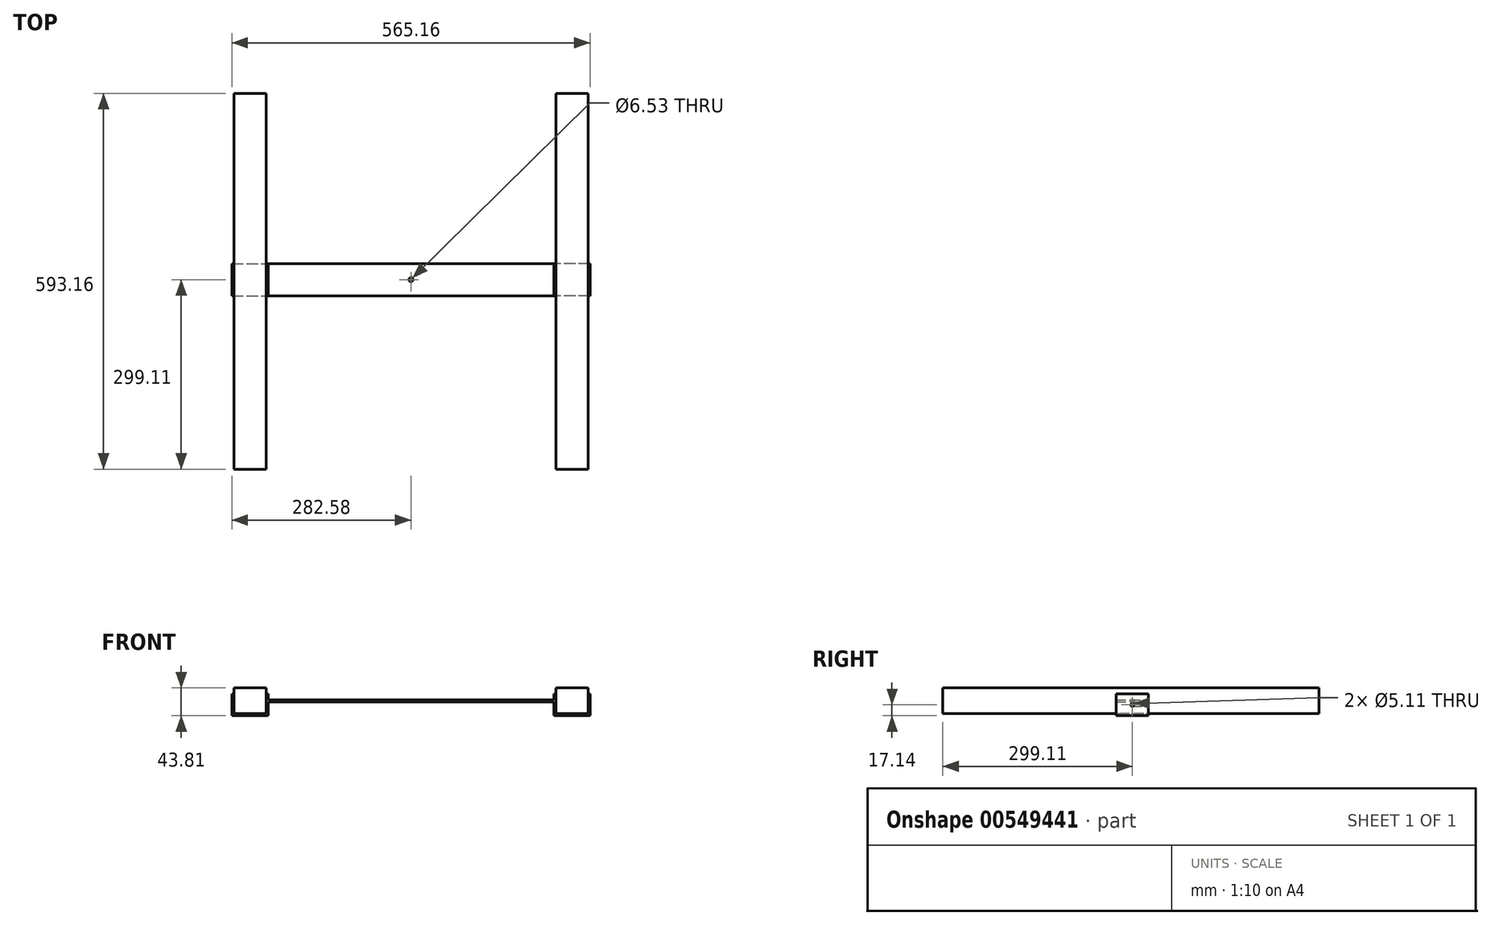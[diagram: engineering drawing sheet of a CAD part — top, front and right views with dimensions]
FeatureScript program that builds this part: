
annotation { "Feature Type Name" : "Feature", "Feature Type Description" : "" }
export const myFeature = defineFeature(function(context is Context, id is Id, definition is map)
    precondition{}
    {
        {
            var Q0;
            Q0=qCreatedBy(makeId("Top.planeOp"),FACE);
            var sketch = newSketch(context, id + "F0", { "sketchPlane" : qUnion([Q0])});
            skLineSegment(sketch, "E0.bottom", {"start": v(-279.4, 294.05) * mm, "end": v(-228.6, 294.05) * mm});
            skLineSegment(sketch, "E0.top", {"start": v(-279.4, -299.1) * mm, "end": v(-228.6, -299.1) * mm});
            skLineSegment(sketch, "E0.left", {"start": v(-279.4, 294.05) * mm, "end": v(-279.4, -299.1) * mm});
            skLineSegment(sketch, "E0.right", {"start": v(-228.6, 294.05) * mm, "end": v(-228.6, -299.1) * mm});
            skLineSegment(sketch, "E1.MirrorCS", {"start": v(279.4, 294.05) * mm, "end": v(228.6, 294.05) * mm});
            skLineSegment(sketch, "E2.MirrorCS", {"start": v(228.6, 294.05) * mm, "end": v(228.6, -299.1) * mm});
            skLineSegment(sketch, "E3.MirrorCS", {"start": v(279.4, 294.05) * mm, "end": v(279.4, -299.1) * mm});
            skLineSegment(sketch, "E4.MirrorCS", {"start": v(279.4, -299.1) * mm, "end": v(228.6, -299.1) * mm});
            skSolve(sketch);
        }
        {
            var Q0;
            Q0 = qSketchRegion(id + "F0", true);
            extrude(context, id + "F1", {"entities" : qUnion([Q0]), "depth" : 40.64 * mm, "offsetDistance" : 25.4 * mm});
        }
        {
            var Q0;
            Q0=qCreatedBy(makeId("Front.planeOp"),FACE);
            var sketch = newSketch(context, id + "F2", { "sketchPlane" : qUnion([Q0])});
            skLineSegment(sketch, "E5.0.0", {"start": v(-279.4, 0) * mm, "end": v(-228.6, 0) * mm});
            skLineSegment(sketch, "E5.0.1", {"start": v(-228.6, 0) * mm, "end": v(-228.6, 40.64) * mm});
            skLineSegment(sketch, "E5.0.2", {"start": v(-228.6, 40.64) * mm, "end": v(-279.4, 40.64) * mm});
            skLineSegment(sketch, "E5.0.3", {"start": v(-279.4, 40.64) * mm, "end": v(-279.4, 0) * mm});
            skLineSegment(sketch, "E6.0", {"start": v(-225.43, -3.17) * mm, "end": v(-225.43, 31.12) * mm});
            skLineSegment(sketch, "E6.1", {"start": v(-282.57, -3.17) * mm, "end": v(-225.43, -3.17) * mm});
            skLineSegment(sketch, "E6.2", {"start": v(-282.57, 31.12) * mm, "end": v(-282.57, -3.17) * mm});
            skLineSegment(sketch, "E7", {"start": v(-282.57, 31.12) * mm, "end": v(-279.4, 31.12) * mm});
            skLineSegment(sketch, "E8", {"start": v(-228.6, 31.12) * mm, "end": v(-225.43, 31.12) * mm});
            skLineSegment(sketch, "E9.MirrorCS", {"start": v(282.57, 31.12) * mm, "end": v(279.4, 31.12) * mm});
            skLineSegment(sketch, "E10.MirrorCS", {"start": v(282.57, 31.12) * mm, "end": v(282.57, -3.17) * mm});
            skLineSegment(sketch, "E11.MirrorCS", {"start": v(228.6, 31.12) * mm, "end": v(225.43, 31.12) * mm});
            skLineSegment(sketch, "E12.MirrorCS", {"start": v(225.43, -3.17) * mm, "end": v(225.43, 31.12) * mm});
            skLineSegment(sketch, "E13.MirrorCS", {"start": v(282.57, -3.17) * mm, "end": v(225.43, -3.17) * mm});
            skLineSegment(sketch, "E14", {"start": v(-225.43, 21.6) * mm, "end": v(225.43, 21.6) * mm});
            skPoint(sketch, "E14.endSnap0", {"position": v(225.43, 13.97) * mm});
            skLineSegment(sketch, "E15.0", {"start": v(-225.43, 18.42) * mm, "end": v(225.43, 18.42) * mm});
            skLineSegment(sketch, "E16.MirrorCS", {"start": v(228.6, 0) * mm, "end": v(228.6, 40.64) * mm});
            skLineSegment(sketch, "E17.MirrorCS", {"start": v(279.4, 0) * mm, "end": v(228.6, 0) * mm});
            skLineSegment(sketch, "E18.MirrorCS", {"start": v(279.4, 40.64) * mm, "end": v(279.4, 0) * mm});
            skSolve(sketch);
        }
        {
            var Q0;
            {var subQ0=sQuery(id+"F2.wireOp",EDGE,"E14");Q0=makeQuery(id+"F2.imprint","IMPRINT",FACE,{"disambiguationData":[TD([[makeQuery(id+"F2.imprint","IMPRINT",EDGE,{"derivedFrom":subQ0}),-1.0]])]});}
            var Q1;
            {var subQ4=sQuery(id+"F2.wireOp",EDGE,"E5.0.0");Q1=makeQuery(id+"F2.imprint","IMPRINT",FACE,{"disambiguationData":[TD([[makeQuery(id+"F2.imprint","IMPRINT",EDGE,{"derivedFrom":subQ4}),-1.0]])]});}
            var Q2;
            {var subQ4=sQuery(id+"F2.wireOp",EDGE,"E9.MirrorCS");Q2=makeQuery(id+"F2.imprint","IMPRINT",FACE,{"disambiguationData":[TD([[makeQuery(id+"F2.imprint","IMPRINT",EDGE,{"derivedFrom":subQ4}),1.0]])]});}
            extrude(context, id + "F3", {"entities" : qUnion([Q0, Q1, Q2]), "depth" : 50.8 * mm, "offsetDistance" : 25.4 * mm, "symmetric" : true});
        }
        {
            var Q0;
            Q0=makeQuery(id+"F3.opExtrude","SWEPT_FACE",FACE,{"disambiguationData":[OSD([sQuery(id+"F2.wireOp",EDGE,"E15.0")])]});
            var sketch = newSketch(context, id + "F4", { "sketchPlane" : qUnion([Q0])});
            skPoint(sketch, "E19", {"position": v(0, 0) * mm});
            skSolve(sketch);
        }
        {
            var Q0;
            Q0=sQuery(id+"F4.wireOp",VERTEX,"E19");
            var Q1;
            Q1=makeQuery(id+"F3.opExtrude","SWEPT_BODY",BODY,{"disambiguationData":[OSD([sQuery(id+"F2.wireOp",EDGE,"E5.0.0"),sQuery(id+"F2.wireOp",EDGE,"E5.0.1"),sQuery(id+"F2.wireOp",EDGE,"E5.0.3"),sQuery(id+"F2.wireOp",EDGE,"E6.0"),sQuery(id+"F2.wireOp",EDGE,"E6.1"),sQuery(id+"F2.wireOp",EDGE,"E6.2"),sQuery(id+"F2.wireOp",EDGE,"E7"),sQuery(id+"F2.wireOp",EDGE,"E8"),sQuery(id+"F2.wireOp",EDGE,"E9.MirrorCS"),sQuery(id+"F2.wireOp",EDGE,"E10.MirrorCS"),sQuery(id+"F2.wireOp",EDGE,"E11.MirrorCS"),sQuery(id+"F2.wireOp",EDGE,"E12.MirrorCS"),sQuery(id+"F2.wireOp",EDGE,"E13.MirrorCS"),sQuery(id+"F2.wireOp",EDGE,"E14"),sQuery(id+"F2.wireOp",EDGE,"E15.0"),sQuery(id+"F2.wireOp",EDGE,"E16.MirrorCS"),sQuery(id+"F2.wireOp",EDGE,"E17.MirrorCS"),sQuery(id+"F2.wireOp",EDGE,"E18.MirrorCS")])]});
            hole(context, id + "F5", {"style" : HoleStyle.SIMPLE, "endStyle" : HoleEndStyle.BLIND, "standardTappedOrClearance" : lookupTablePath({ "standard" : "ANSI", "engagement" : "75%", "pitch" : "18 tpi", "size" : "5/16", "type" : "Tapped" }), "standardBlindInLast" : lookupTablePath({ "standard" : "ANSI", "engagement" : "75%", "pitch" : "18 tpi", "size" : "5/16", "type" : "Tapped" }), "holeDiameter" : 6.53 * mm, "majorDiameter" : 7.94 * mm, "showTappedDepth" : true, "holeDepth" : 48.69 * mm, "isTappedThrough" : true, "tappedDepth" : 44.46 * mm, "tapClearance" : 3, "startFromSketch" : true, "locations" : qUnion([Q0]), "scope" : qUnion([Q1])});
        }
        {
            var Q0;
            Q0=makeQuery(id+"F3.opExtrude","SWEPT_FACE",FACE,{"disambiguationData":[OSD([sQuery(id+"F2.wireOp",EDGE,"E6.2")])]});
            var sketch = newSketch(context, id + "F6", { "sketchPlane" : qUnion([Q0])});
            skLineSegment(sketch, "E20.0.0", {"start": v(-25.4, 31.12) * mm, "end": v(-25.4, -3.17) * mm});
            skLineSegment(sketch, "E20.0.1", {"start": v(-25.4, -3.17) * mm, "end": v(25.4, -3.17) * mm});
            skLineSegment(sketch, "E20.0.2", {"start": v(25.4, -3.17) * mm, "end": v(25.4, 31.12) * mm});
            skLineSegment(sketch, "E20.0.3", {"start": v(25.4, 31.12) * mm, "end": v(-25.4, 31.12) * mm});
            skPoint(sketch, "E21", {"position": v(0, 13.97) * mm});
            skPoint(sketch, "E21.positionSnap0", {"position": v(-25.4, 13.97) * mm});
            skSolve(sketch);
        }
        {
            var Q0;
            Q0=sQuery(id+"F6.wireOp",VERTEX,"E21");
            var Q1;
            Q1=makeQuery(id+"F3.opExtrude","SWEPT_BODY",BODY,{"disambiguationData":[OSD([sQuery(id+"F2.wireOp",EDGE,"E5.0.0"),sQuery(id+"F2.wireOp",EDGE,"E5.0.1"),sQuery(id+"F2.wireOp",EDGE,"E5.0.3"),sQuery(id+"F2.wireOp",EDGE,"E6.0"),sQuery(id+"F2.wireOp",EDGE,"E6.1"),sQuery(id+"F2.wireOp",EDGE,"E6.2"),sQuery(id+"F2.wireOp",EDGE,"E7"),sQuery(id+"F2.wireOp",EDGE,"E8"),sQuery(id+"F2.wireOp",EDGE,"E9.MirrorCS"),sQuery(id+"F2.wireOp",EDGE,"E10.MirrorCS"),sQuery(id+"F2.wireOp",EDGE,"E11.MirrorCS"),sQuery(id+"F2.wireOp",EDGE,"E12.MirrorCS"),sQuery(id+"F2.wireOp",EDGE,"E13.MirrorCS"),sQuery(id+"F2.wireOp",EDGE,"E14"),sQuery(id+"F2.wireOp",EDGE,"E15.0"),sQuery(id+"F2.wireOp",EDGE,"E16.MirrorCS"),sQuery(id+"F2.wireOp",EDGE,"E17.MirrorCS"),sQuery(id+"F2.wireOp",EDGE,"E18.MirrorCS")])]});
            hole(context, id + "F7", {"style" : HoleStyle.SIMPLE, "endStyle" : HoleEndStyle.BLIND, "standardTappedOrClearance" : lookupTablePath({ "standard" : "ANSI", "engagement" : "75%", "pitch" : "20 tpi", "size" : "1/4", "type" : "Tapped" }), "standardBlindInLast" : lookupTablePath({ "standard" : "ANSI", "engagement" : "75%", "pitch" : "20 tpi", "size" : "1/4", "type" : "Tapped" }), "holeDiameter" : 5.1 * mm, "majorDiameter" : 6.35 * mm, "showTappedDepth" : true, "holeDepth" : 48.27 * mm, "isTappedThrough" : true, "tappedDepth" : 44.46 * mm, "tapClearance" : 3, "startFromSketch" : true, "locations" : qUnion([Q0]), "scope" : qUnion([Q1])});
        }
        {
            var Q0;
            Q0=makeQuery(id+"F3.opExtrude","SWEPT_FACE",FACE,{"disambiguationData":[OSD([sQuery(id+"F2.wireOp",EDGE,"E10.MirrorCS")])]});
            var sketch = newSketch(context, id + "F8", { "sketchPlane" : qUnion([Q0])});
            skPoint(sketch, "E22", {"position": v(0, 13.97) * mm});
            skPoint(sketch, "E22.positionSnap0", {"position": v(-25.4, 13.97) * mm});
            skSolve(sketch);
        }
        {
            var Q0;
            Q0=sQuery(id+"F2.wireOp",VERTEX,"E14.endSnap0");
            var Q1;
            Q1=sQuery(id+"F8.wireOp",VERTEX,"E22");
            var Q2;
            Q2=makeQuery(id+"F3.opExtrude","SWEPT_BODY",BODY,{"disambiguationData":[OSD([sQuery(id+"F2.wireOp",EDGE,"E5.0.0"),sQuery(id+"F2.wireOp",EDGE,"E5.0.1"),sQuery(id+"F2.wireOp",EDGE,"E5.0.3"),sQuery(id+"F2.wireOp",EDGE,"E6.0"),sQuery(id+"F2.wireOp",EDGE,"E6.1"),sQuery(id+"F2.wireOp",EDGE,"E6.2"),sQuery(id+"F2.wireOp",EDGE,"E7"),sQuery(id+"F2.wireOp",EDGE,"E8"),sQuery(id+"F2.wireOp",EDGE,"E9.MirrorCS"),sQuery(id+"F2.wireOp",EDGE,"E10.MirrorCS"),sQuery(id+"F2.wireOp",EDGE,"E11.MirrorCS"),sQuery(id+"F2.wireOp",EDGE,"E12.MirrorCS"),sQuery(id+"F2.wireOp",EDGE,"E13.MirrorCS"),sQuery(id+"F2.wireOp",EDGE,"E14"),sQuery(id+"F2.wireOp",EDGE,"E15.0"),sQuery(id+"F2.wireOp",EDGE,"E16.MirrorCS"),sQuery(id+"F2.wireOp",EDGE,"E17.MirrorCS"),sQuery(id+"F2.wireOp",EDGE,"E18.MirrorCS")])]});
            hole(context, id + "F9", {"style" : HoleStyle.SIMPLE, "endStyle" : HoleEndStyle.BLIND, "standardTappedOrClearance" : lookupTablePath({ "standard" : "ANSI", "engagement" : "75%", "pitch" : "20 tpi", "size" : "1/4", "type" : "Tapped" }), "standardBlindInLast" : lookupTablePath({ "standard" : "ANSI", "engagement" : "75%", "pitch" : "20 tpi", "size" : "1/4", "type" : "Tapped" }), "holeDiameter" : 5.1 * mm, "majorDiameter" : 6.35 * mm, "showTappedDepth" : true, "holeDepth" : 48.26 * mm, "isTappedThrough" : true, "tappedDepth" : 44.45 * mm, "tapClearance" : 3, "startFromSketch" : true, "locations" : qUnion([Q0, Q1]), "scope" : qUnion([Q2])});
        }
    });
